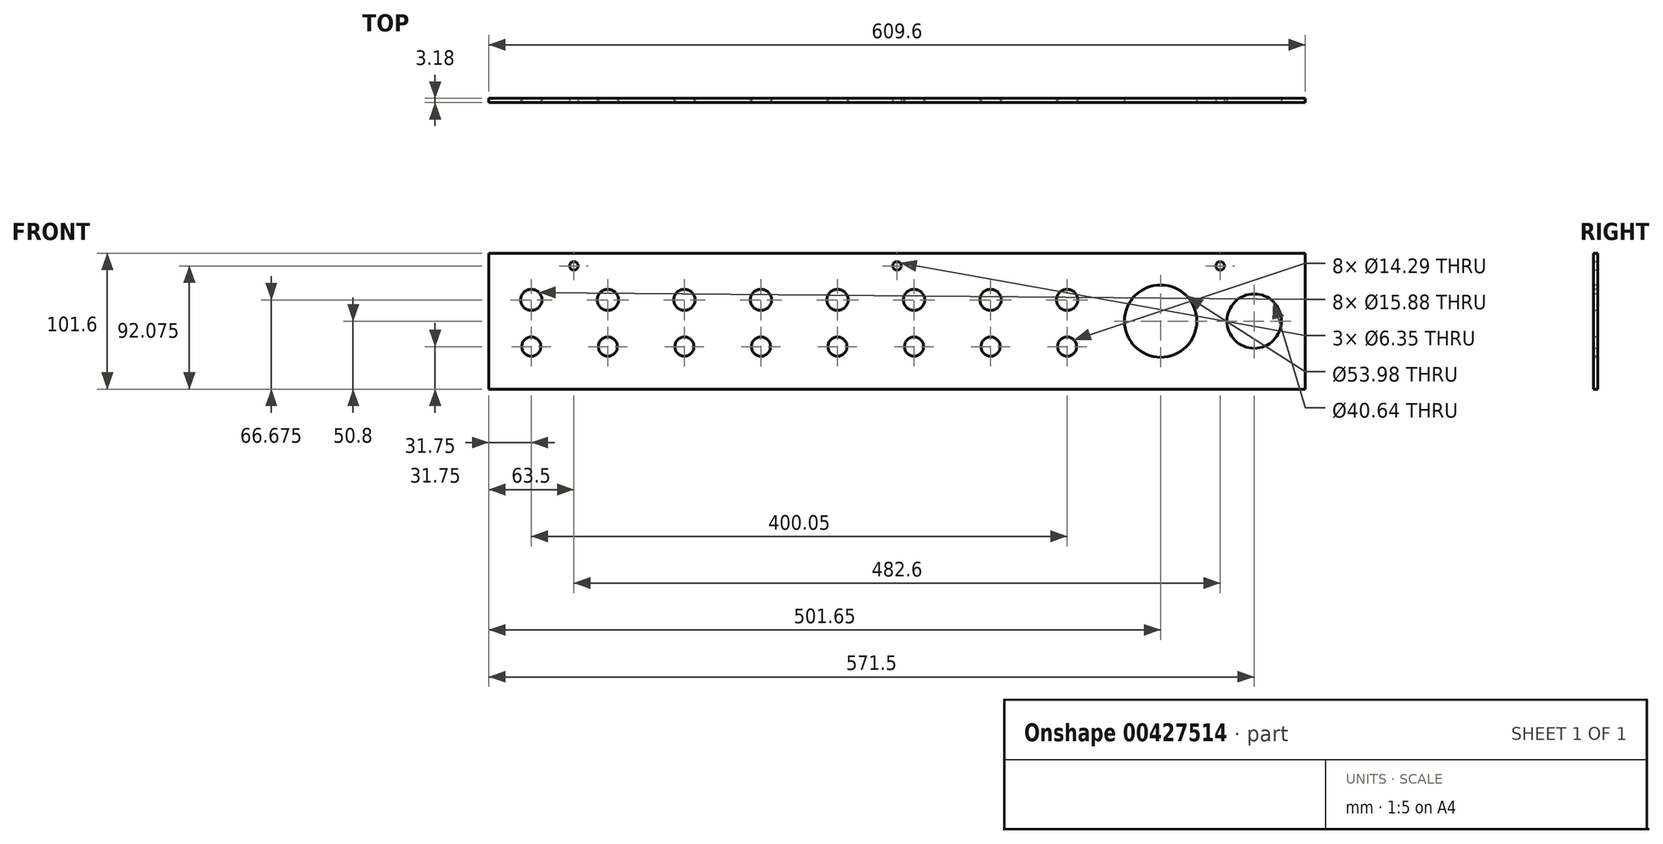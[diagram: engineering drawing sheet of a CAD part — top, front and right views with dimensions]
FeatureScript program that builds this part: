
annotation { "Feature Type Name" : "Feature", "Feature Type Description" : "" }
export const myFeature = defineFeature(function(context is Context, id is Id, definition is map)
    precondition{}
    {
        {
            var Q0;
            Q0=qCreatedBy(makeId("Front.planeOp"),FACE);
            var sketch = newSketch(context, id + "F0", { "sketchPlane" : qUnion([Q0])});
            skLineSegment(sketch, "E0.bottom", {"start": v(0, 0) * mm, "end": v(609.6, 0) * mm});
            skLineSegment(sketch, "E0.top", {"start": v(0, 101.6) * mm, "end": v(609.6, 101.6) * mm});
            skLineSegment(sketch, "E0.left", {"start": v(0, 0) * mm, "end": v(0, 101.6) * mm});
            skLineSegment(sketch, "E0.right", {"start": v(609.6, 0) * mm, "end": v(609.6, 101.6) * mm});
            skSolve(sketch);
        }
        {
            var Q0;
            Q0=qSketchRegion(id+"F0",true);
            extrude(context, id + "F1", {"entities" : qUnion([Q0]), "depth" : 3.17 * mm});
        }
        {
            var Q0;
            Q0=makeQuery(id+"F1.opExtrude","CAP_FACE",FACE,{"disambiguationData":[OSD([sQuery(id+"F0.wireOp",EDGE,"E0.bottom"),sQuery(id+"F0.wireOp",EDGE,"E0.top"),sQuery(id+"F0.wireOp",EDGE,"E0.left"),sQuery(id+"F0.wireOp",EDGE,"E0.right")])],"isStart":false});
            var sketch = newSketch(context, id + "F2", { "sketchPlane" : qUnion([Q0])});
            skCircle(sketch, "E1", {"center": v(31.75, 31.75) * mm, "radius": 7.14 * mm});
            skCircle(sketch, "E2.1.0.0", {"center": v(88.9, 31.75) * mm, "radius": 7.14 * mm});
            skCircle(sketch, "E2.2.0.0", {"center": v(146.05, 31.75) * mm, "radius": 7.14 * mm});
            skCircle(sketch, "E2.3.0.0", {"center": v(203.2, 31.75) * mm, "radius": 7.14 * mm});
            skCircle(sketch, "E2.4.0.0", {"center": v(260.35, 31.75) * mm, "radius": 7.14 * mm});
            skCircle(sketch, "E2.5.0.0", {"center": v(317.5, 31.75) * mm, "radius": 7.14 * mm});
            skCircle(sketch, "E2.6.0.0", {"center": v(374.65, 31.75) * mm, "radius": 7.14 * mm});
            skCircle(sketch, "E2.7.0.0", {"center": v(431.8, 31.75) * mm, "radius": 7.14 * mm});
            skLineSegment(sketch, "E2.direction1", {"start": v(31.75, 31.75) * mm, "end": v(88.9, 31.75) * mm, "construction": true});
            skSolve(sketch);
        }
        {
            var Q0;
            Q0=qSketchRegion(id+"F2",true);
            extrude(context, id + "F3", {"entities" : qUnion([Q0]), "operationType" : NewBodyOperationType.REMOVE, "endBound" : BoundingType.THROUGH_ALL, "oppositeDirection" : true, "depth" : 25.4 * mm});
        }
        {
            var Q0;
            Q0=makeQuery(id+"F1.opExtrude","CAP_FACE",FACE,{"disambiguationData":[OSD([sQuery(id+"F0.wireOp",EDGE,"E0.bottom"),sQuery(id+"F0.wireOp",EDGE,"E0.top"),sQuery(id+"F0.wireOp",EDGE,"E0.left"),sQuery(id+"F0.wireOp",EDGE,"E0.right")])],"isStart":false});
            var sketch = newSketch(context, id + "F4", { "sketchPlane" : qUnion([Q0])});
            skCircle(sketch, "E3", {"center": v(501.65, 50.8) * mm, "radius": 26.99 * mm});
            skSolve(sketch);
        }
        {
            var Q0;
            Q0=qSketchRegion(id+"F4",true);
            extrude(context, id + "F5", {"entities" : qUnion([Q0]), "operationType" : NewBodyOperationType.REMOVE, "endBound" : BoundingType.THROUGH_ALL, "oppositeDirection" : true, "depth" : 25.4 * mm});
        }
        {
            var Q0;
            Q0=makeQuery(id+"F1.opExtrude","CAP_FACE",FACE,{"disambiguationData":[OSD([sQuery(id+"F0.wireOp",EDGE,"E0.bottom"),sQuery(id+"F0.wireOp",EDGE,"E0.top"),sQuery(id+"F0.wireOp",EDGE,"E0.left"),sQuery(id+"F0.wireOp",EDGE,"E0.right")])],"isStart":false});
            var sketch = newSketch(context, id + "F6", { "sketchPlane" : qUnion([Q0])});
            skCircle(sketch, "E4", {"center": v(571.5, 50.8) * mm, "radius": 20.32 * mm});
            skSolve(sketch);
        }
        {
            var Q0;
            Q0=makeQuery(id+"F6.imprint","IMPRINT",FACE,{"disambiguationData":[TD([[makeQuery(id+"F6.imprint","IMPRINT",EDGE,{"derivedFrom":sQuery(id+"F6.wireOp",EDGE,"E4")}),1.0]])]});
            extrude(context, id + "F7", {"entities" : qUnion([Q0]), "operationType" : NewBodyOperationType.REMOVE, "endBound" : BoundingType.THROUGH_ALL, "oppositeDirection" : true, "depth" : 25.4 * mm});
        }
        {
            var Q0;
            Q0=makeQuery(id+"F1.opExtrude","CAP_FACE",FACE,{"disambiguationData":[OSD([sQuery(id+"F0.wireOp",EDGE,"E0.bottom"),sQuery(id+"F0.wireOp",EDGE,"E0.top"),sQuery(id+"F0.wireOp",EDGE,"E0.left"),sQuery(id+"F0.wireOp",EDGE,"E0.right")])],"isStart":false});
            var sketch = newSketch(context, id + "F8", { "sketchPlane" : qUnion([Q0])});
            skCircle(sketch, "E5", {"center": v(31.75, 66.68) * mm, "radius": 7.94 * mm});
            skCircle(sketch, "E6.1.0.0", {"center": v(88.9, 66.68) * mm, "radius": 7.94 * mm});
            skCircle(sketch, "E6.2.0.0", {"center": v(146.05, 66.68) * mm, "radius": 7.94 * mm});
            skCircle(sketch, "E6.3.0.0", {"center": v(203.2, 66.68) * mm, "radius": 7.94 * mm});
            skCircle(sketch, "E6.4.0.0", {"center": v(260.35, 66.68) * mm, "radius": 7.94 * mm});
            skCircle(sketch, "E6.5.0.0", {"center": v(317.5, 66.68) * mm, "radius": 7.94 * mm});
            skCircle(sketch, "E6.6.0.0", {"center": v(374.65, 66.68) * mm, "radius": 7.94 * mm});
            skCircle(sketch, "E6.7.0.0", {"center": v(431.8, 66.68) * mm, "radius": 7.94 * mm});
            skLineSegment(sketch, "E6.direction1", {"start": v(31.75, 66.68) * mm, "end": v(88.9, 66.68) * mm, "construction": true});
            skSolve(sketch);
        }
        {
            var Q0;
            Q0=makeQuery(id+"F8.imprint","IMPRINT",FACE,{"disambiguationData":[TD([[makeQuery(id+"F8.imprint","IMPRINT",EDGE,{"derivedFrom":sQuery(id+"F8.wireOp",EDGE,"E5")}),1.0]])]});
            var Q1;
            Q1=makeQuery(id+"F8.imprint","IMPRINT",FACE,{"disambiguationData":[TD([[makeQuery(id+"F8.imprint","IMPRINT",EDGE,{"derivedFrom":sQuery(id+"F8.wireOp",EDGE,"E6.1.0.0")}),1.0]])]});
            var Q2;
            Q2=makeQuery(id+"F8.imprint","IMPRINT",FACE,{"disambiguationData":[TD([[makeQuery(id+"F8.imprint","IMPRINT",EDGE,{"derivedFrom":sQuery(id+"F8.wireOp",EDGE,"E6.2.0.0")}),1.0]])]});
            var Q3;
            Q3=makeQuery(id+"F8.imprint","IMPRINT",FACE,{"disambiguationData":[TD([[makeQuery(id+"F8.imprint","IMPRINT",EDGE,{"derivedFrom":sQuery(id+"F8.wireOp",EDGE,"E6.3.0.0")}),1.0]])]});
            var Q4;
            Q4=makeQuery(id+"F8.imprint","IMPRINT",FACE,{"disambiguationData":[TD([[makeQuery(id+"F8.imprint","IMPRINT",EDGE,{"derivedFrom":sQuery(id+"F8.wireOp",EDGE,"E6.4.0.0")}),1.0]])]});
            var Q5;
            Q5=makeQuery(id+"F8.imprint","IMPRINT",FACE,{"disambiguationData":[TD([[makeQuery(id+"F8.imprint","IMPRINT",EDGE,{"derivedFrom":sQuery(id+"F8.wireOp",EDGE,"E6.5.0.0")}),1.0]])]});
            var Q6;
            Q6=makeQuery(id+"F8.imprint","IMPRINT",FACE,{"disambiguationData":[TD([[makeQuery(id+"F8.imprint","IMPRINT",EDGE,{"derivedFrom":sQuery(id+"F8.wireOp",EDGE,"E6.6.0.0")}),1.0]])]});
            var Q7;
            Q7=makeQuery(id+"F8.imprint","IMPRINT",FACE,{"disambiguationData":[TD([[makeQuery(id+"F8.imprint","IMPRINT",EDGE,{"derivedFrom":sQuery(id+"F8.wireOp",EDGE,"E6.7.0.0")}),1.0]])]});
            extrude(context, id + "F9", {"entities" : qUnion([Q0, Q1, Q2, Q3, Q4, Q5, Q6, Q7]), "operationType" : NewBodyOperationType.REMOVE, "endBound" : BoundingType.THROUGH_ALL, "oppositeDirection" : true, "depth" : 25.4 * mm});
        }
        {
            var Q0;
            Q0=makeQuery(id+"F1.opExtrude","CAP_FACE",FACE,{"disambiguationData":[OSD([sQuery(id+"F0.wireOp",EDGE,"E0.bottom"),sQuery(id+"F0.wireOp",EDGE,"E0.top"),sQuery(id+"F0.wireOp",EDGE,"E0.left"),sQuery(id+"F0.wireOp",EDGE,"E0.right")])],"isStart":false});
            var sketch = newSketch(context, id + "F10", { "sketchPlane" : qUnion([Q0])});
            skCircle(sketch, "E7", {"center": v(63.5, 92.08) * mm, "radius": 3.18 * mm});
            skCircle(sketch, "E8.1.0.0", {"center": v(304.8, 92.08) * mm, "radius": 3.18 * mm});
            skCircle(sketch, "E8.2.0.0", {"center": v(546.1, 92.08) * mm, "radius": 3.18 * mm});
            skLineSegment(sketch, "E8.direction1", {"start": v(63.5, 92.08) * mm, "end": v(304.8, 92.08) * mm, "construction": true});
            skSolve(sketch);
        }
        {
            var Q0;
            Q0=makeQuery(id+"F10.imprint","IMPRINT",FACE,{"disambiguationData":[TD([[makeQuery(id+"F10.imprint","IMPRINT",EDGE,{"derivedFrom":sQuery(id+"F10.wireOp",EDGE,"E7")}),1.0]])]});
            var Q1;
            Q1=makeQuery(id+"F10.imprint","IMPRINT",FACE,{"disambiguationData":[TD([[makeQuery(id+"F10.imprint","IMPRINT",EDGE,{"derivedFrom":sQuery(id+"F10.wireOp",EDGE,"E8.1.0.0")}),1.0]])]});
            var Q2;
            Q2=makeQuery(id+"F10.imprint","IMPRINT",FACE,{"disambiguationData":[TD([[makeQuery(id+"F10.imprint","IMPRINT",EDGE,{"derivedFrom":sQuery(id+"F10.wireOp",EDGE,"E8.2.0.0")}),1.0]])]});
            var Q3;
            Q3=makeQuery(id+"F10.imprint","IMPRINT",FACE,{"disambiguationData":[TD([[makeQuery(id+"F10.imprint","IMPRINT",EDGE,{"derivedFrom":sQuery(id+"F10.wireOp",EDGE,"E8.3.0.0")}),1.0]])]});
            var Q4;
            Q4=makeQuery(id+"F10.imprint","IMPRINT",FACE,{"disambiguationData":[TD([[makeQuery(id+"F10.imprint","IMPRINT",EDGE,{"derivedFrom":sQuery(id+"F10.wireOp",EDGE,"E8.4.0.0")}),1.0]])]});
            extrude(context, id + "F11", {"entities" : qUnion([Q0, Q1, Q2, Q3, Q4]), "operationType" : NewBodyOperationType.REMOVE, "endBound" : BoundingType.THROUGH_ALL, "oppositeDirection" : true, "depth" : 25.4 * mm});
        }
    });
